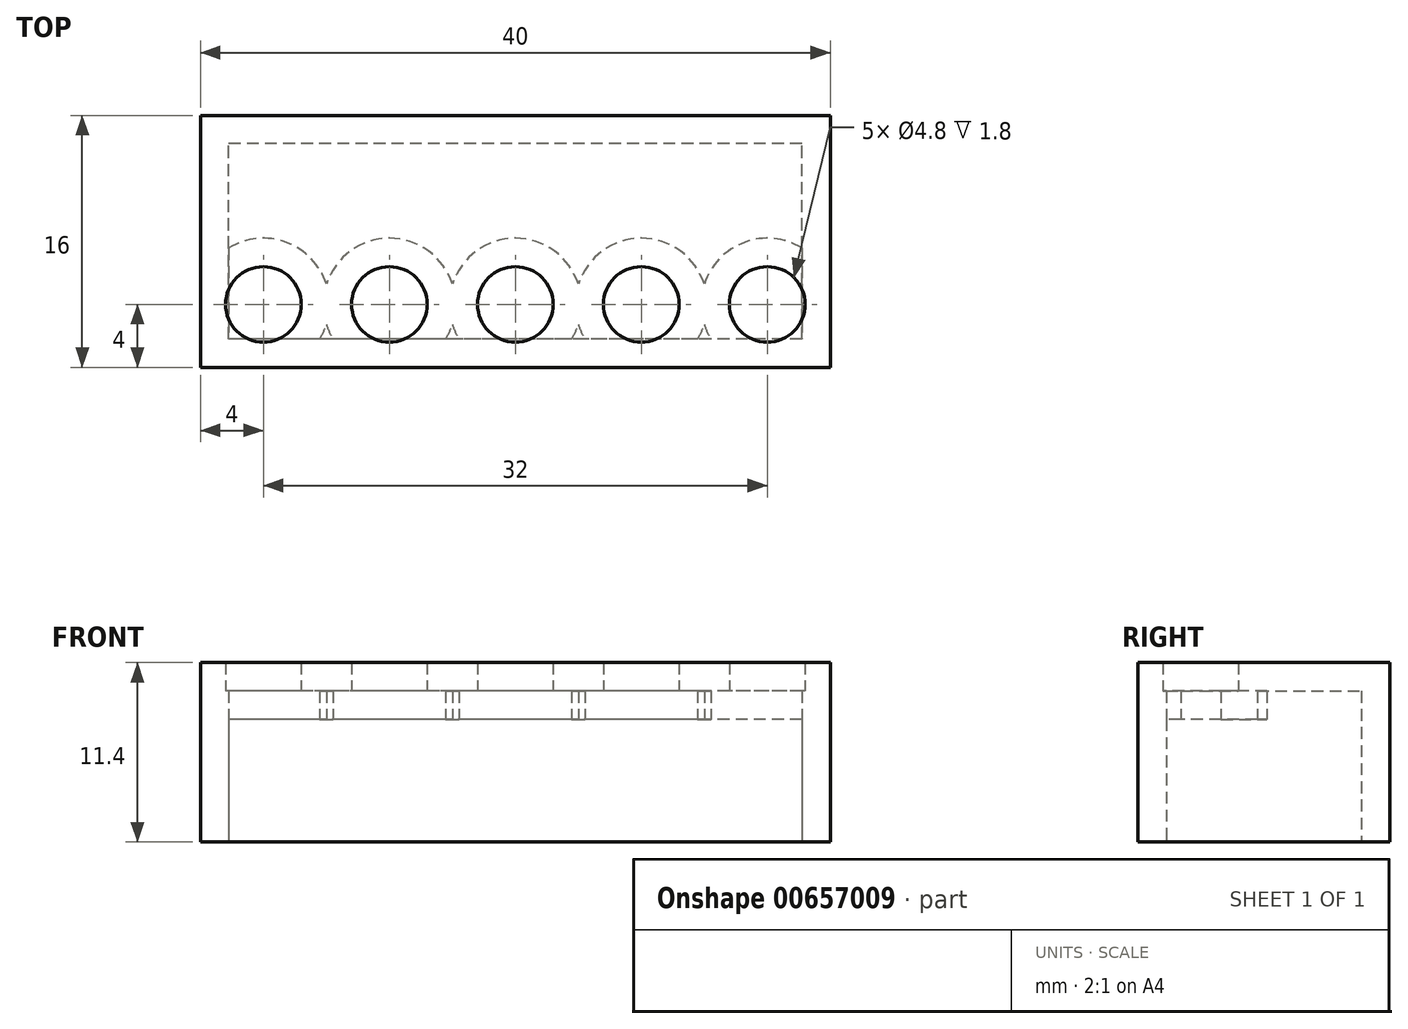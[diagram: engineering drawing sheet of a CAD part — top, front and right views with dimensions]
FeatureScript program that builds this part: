
annotation { "Feature Type Name" : "Feature", "Feature Type Description" : "" }
export const myFeature = defineFeature(function(context is Context, id is Id, definition is map)
    precondition{}
    {
        {
            var Q0;
            Q0=qCreatedBy(makeId("Top.planeOp"),FACE);
            var sketch = newSketch(context, id + "F0", { "sketchPlane" : qUnion([Q0])});
            skLineSegment(sketch, "E0.bottom", {"start": v(0, 0) * mm, "end": v(-40, 0) * mm});
            skLineSegment(sketch, "E0.top", {"start": v(0, 16) * mm, "end": v(-40, 16) * mm});
            skLineSegment(sketch, "E0.left", {"start": v(0, 0) * mm, "end": v(0, 16) * mm});
            skLineSegment(sketch, "E0.right", {"start": v(-40, 0) * mm, "end": v(-40, 16) * mm});
            skSolve(sketch);
        }
        {
            var Q0;
            Q0=makeQuery(id+"F0.imprint","IMPRINT",FACE,{"disambiguationData":[TD([[makeQuery(id+"F0.imprint","IMPRINT",EDGE,{"derivedFrom":sQuery(id+"F0.wireOp",EDGE,"E0.bottom")}),-1.0]])]});
            extrude(context, id + "F1", {"entities" : qUnion([Q0]), "depth" : 9.6 * mm, "offsetDistance" : 25.4 * mm});
        }
        {
            var Q0;
            Q0=makeQuery(id+"F1.opExtrude","CAP_FACE",FACE,{"disambiguationData":[OSD([sQuery(id+"F0.wireOp",EDGE,"E0.bottom"),sQuery(id+"F0.wireOp",EDGE,"E0.top"),sQuery(id+"F0.wireOp",EDGE,"E0.left"),sQuery(id+"F0.wireOp",EDGE,"E0.right")])],"isStart":false});
            var sketch = newSketch(context, id + "F2", { "sketchPlane" : qUnion([Q0])});
            skLineSegment(sketch, "E1", {"start": v(-40, 8) * mm, "end": v(0, 8) * mm, "construction": true});
            skLineSegment(sketch, "E2", {"start": v(-32, 16) * mm, "end": v(-32, 0) * mm, "construction": true});
            skLineSegment(sketch, "E3", {"start": v(-24, 16) * mm, "end": v(-24, 0) * mm, "construction": true});
            skLineSegment(sketch, "E4", {"start": v(-16, 16) * mm, "end": v(-16, 0) * mm, "construction": true});
            skLineSegment(sketch, "E5", {"start": v(-8, 16) * mm, "end": v(-8, 0) * mm, "construction": true});
            skLineSegment(sketch, "E6", {"start": v(-40, 16) * mm, "end": v(-32, 8) * mm, "construction": true});
            skLineSegment(sketch, "E7", {"start": v(-32, 8) * mm, "end": v(-24, 16) * mm, "construction": true});
            skLineSegment(sketch, "E8", {"start": v(-24, 16) * mm, "end": v(-16, 8) * mm, "construction": true});
            skLineSegment(sketch, "E9", {"start": v(-16, 8) * mm, "end": v(-8, 16) * mm, "construction": true});
            skLineSegment(sketch, "E10", {"start": v(-8, 16) * mm, "end": v(0, 8) * mm, "construction": true});
            skCircle(sketch, "E11", {"center": v(-36, 12) * mm, "radius": 2.4 * mm});
            skCircle(sketch, "E12", {"center": v(-28, 12) * mm, "radius": 2.4 * mm});
            skCircle(sketch, "E13", {"center": v(-20, 12) * mm, "radius": 2.4 * mm});
            skCircle(sketch, "E14", {"center": v(-12, 12) * mm, "radius": 2.4 * mm});
            skCircle(sketch, "E15", {"center": v(-4, 12) * mm, "radius": 2.4 * mm});
            skCircle(sketch, "E16.MirrorC", {"center": v(-36, 4) * mm, "radius": 2.4 * mm});
            skCircle(sketch, "E17.MirrorC", {"center": v(-28, 4) * mm, "radius": 2.4 * mm});
            skCircle(sketch, "E18.MirrorC", {"center": v(-20, 4) * mm, "radius": 2.4 * mm});
            skCircle(sketch, "E19.MirrorC", {"center": v(-12, 4) * mm, "radius": 2.4 * mm});
            skCircle(sketch, "E20.MirrorC", {"center": v(-4, 4) * mm, "radius": 2.4 * mm});
            skSolve(sketch);
        }
        {
            var Q0;
            Q0=makeQuery(id+"F2.imprint","IMPRINT",FACE,{"disambiguationData":[TD([[makeQuery(id+"F2.imprint","IMPRINT",EDGE,{"derivedFrom":sQuery(id+"F2.wireOp",EDGE,"E11")}),1.0]])]});
            var Q1;
            Q1=makeQuery(id+"F2.imprint","IMPRINT",FACE,{"disambiguationData":[TD([[makeQuery(id+"F2.imprint","IMPRINT",EDGE,{"derivedFrom":sQuery(id+"F2.wireOp",EDGE,"E16.MirrorC")}),-1.0]])]});
            var Q2;
            Q2=makeQuery(id+"F2.imprint","IMPRINT",FACE,{"disambiguationData":[TD([[makeQuery(id+"F2.imprint","IMPRINT",EDGE,{"derivedFrom":sQuery(id+"F2.wireOp",EDGE,"E17.MirrorC")}),-1.0]])]});
            var Q3;
            Q3=makeQuery(id+"F2.imprint","IMPRINT",FACE,{"disambiguationData":[TD([[makeQuery(id+"F2.imprint","IMPRINT",EDGE,{"derivedFrom":sQuery(id+"F2.wireOp",EDGE,"E12")}),1.0]])]});
            var Q4;
            Q4=makeQuery(id+"F2.imprint","IMPRINT",FACE,{"disambiguationData":[TD([[makeQuery(id+"F2.imprint","IMPRINT",EDGE,{"derivedFrom":sQuery(id+"F2.wireOp",EDGE,"E18.MirrorC")}),-1.0]])]});
            var Q5;
            Q5=makeQuery(id+"F2.imprint","IMPRINT",FACE,{"disambiguationData":[TD([[makeQuery(id+"F2.imprint","IMPRINT",EDGE,{"derivedFrom":sQuery(id+"F2.wireOp",EDGE,"E19.MirrorC")}),-1.0]])]});
            var Q6;
            Q6=makeQuery(id+"F2.imprint","IMPRINT",FACE,{"disambiguationData":[TD([[makeQuery(id+"F2.imprint","IMPRINT",EDGE,{"derivedFrom":sQuery(id+"F2.wireOp",EDGE,"E20.MirrorC")}),-1.0]])]});
            var Q7;
            Q7=makeQuery(id+"F2.imprint","IMPRINT",FACE,{"disambiguationData":[TD([[makeQuery(id+"F2.imprint","IMPRINT",EDGE,{"derivedFrom":sQuery(id+"F2.wireOp",EDGE,"E15")}),1.0]])]});
            var Q8;
            Q8=makeQuery(id+"F2.imprint","IMPRINT",FACE,{"disambiguationData":[TD([[makeQuery(id+"F2.imprint","IMPRINT",EDGE,{"derivedFrom":sQuery(id+"F2.wireOp",EDGE,"E14")}),1.0]])]});
            var Q9;
            Q9=makeQuery(id+"F2.imprint","IMPRINT",FACE,{"disambiguationData":[TD([[makeQuery(id+"F2.imprint","IMPRINT",EDGE,{"derivedFrom":sQuery(id+"F2.wireOp",EDGE,"E13")}),1.0]])]});
            extrude(context, id + "F3", {"entities" : qUnion([Q0, Q1, Q2, Q3, Q4, Q5, Q6, Q7, Q8, Q9]), "operationType" : NewBodyOperationType.ADD, "depth" : 1.8 * mm, "offsetDistance" : 25.4 * mm});
        }
        {
            var Q0;
            Q0=makeQuery(id+"F1.opExtrude","CAP_FACE",FACE,{"disambiguationData":[OSD([sQuery(id+"F0.wireOp",EDGE,"E0.bottom"),sQuery(id+"F0.wireOp",EDGE,"E0.top"),sQuery(id+"F0.wireOp",EDGE,"E0.left"),sQuery(id+"F0.wireOp",EDGE,"E0.right")])],"isStart":true});
            shell(context, id + "F4", {"entities" : qUnion([Q0]), "thickness" : 1.8 * mm});
        }
    });
